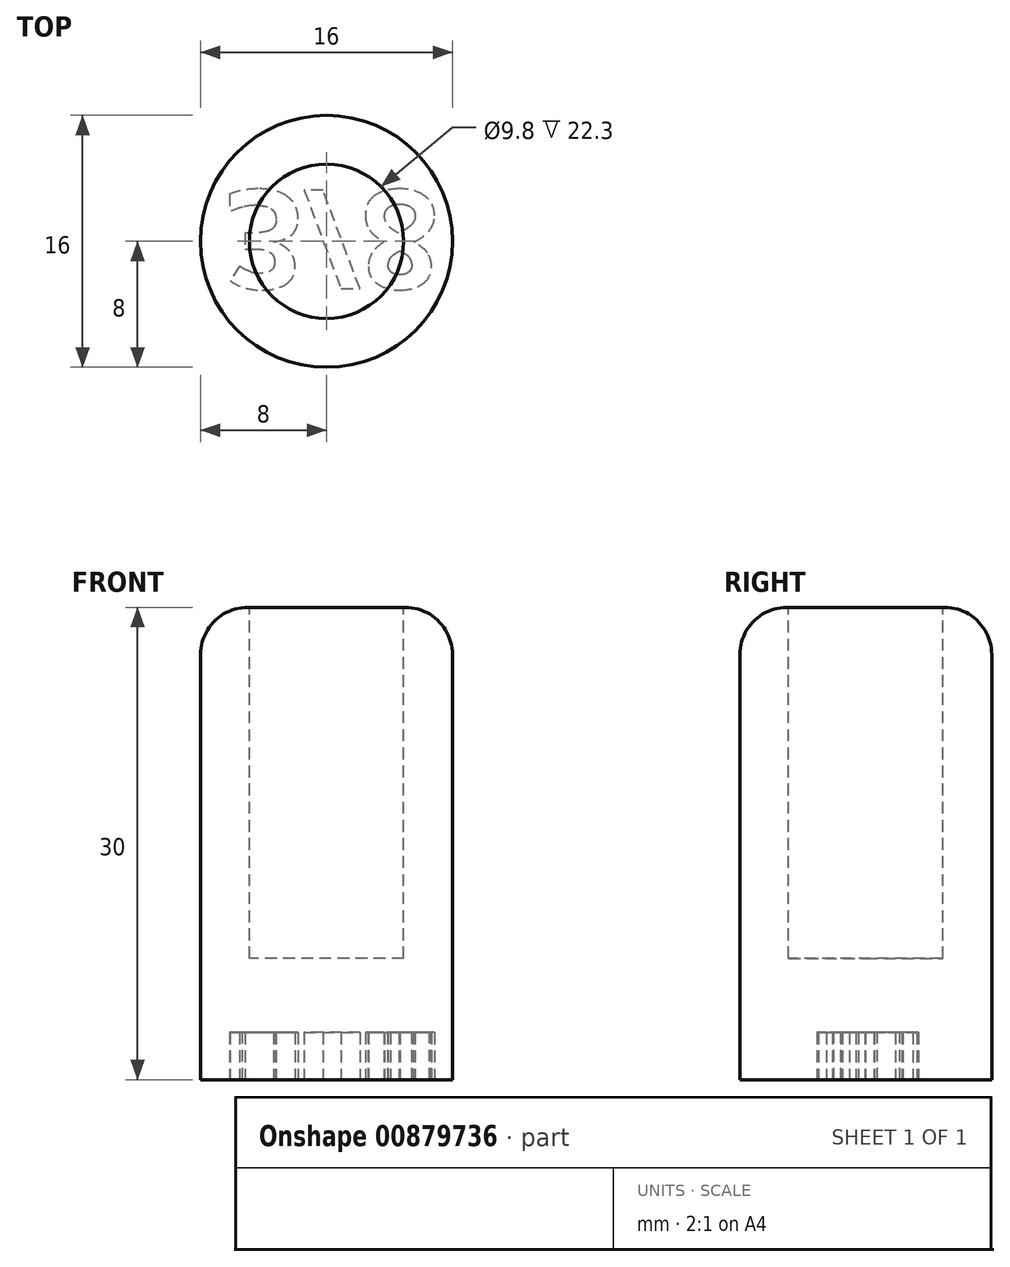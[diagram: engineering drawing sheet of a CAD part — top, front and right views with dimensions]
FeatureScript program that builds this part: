
annotation { "Feature Type Name" : "Feature", "Feature Type Description" : "" }
export const myFeature = defineFeature(function(context is Context, id is Id, definition is map)
    precondition{}
    {
        {
            var Q0;
            Q0=qCreatedBy(makeId("Top.planeOp"),FACE);
            var sketch = newSketch(context, id + "F0", { "sketchPlane" : qUnion([Q0])});
            skCircle(sketch, "E0", {"center": v(0, 0) * mm, "radius": 8 * mm});
            skSolve(sketch);
        }
        {
            var Q0;
            Q0=makeQuery(id+"F0.imprint","IMPRINT",FACE,{"disambiguationData":[TD([[makeQuery(id+"F0.imprint","IMPRINT",EDGE,{"derivedFrom":sQuery(id+"F0.wireOp",EDGE,"E0")}),1.0]])]});
            extrude(context, id + "F1", {"entities" : qUnion([Q0]), "depth" : 30 * mm, "offsetDistance" : 25 * mm});
        }
        {
            var Q0;
            Q0=makeQuery(id+"F1.opExtrude","CAP_FACE",FACE,{"disambiguationData":[OSD([sQuery(id+"F0.wireOp",EDGE,"E0")])],"isStart":false});
            cPlane(context, id + "F2", {"entities" : qUnion([Q0]), "cplaneType" : CPlaneType.OFFSET, "offset" : 0 * mm, "width" : 150 * mm, "height" : 150 * mm});
        }
        {
            var Q0;
            Q0=qCreatedBy(id+"F2.planeOp",FACE);
            var sketch = newSketch(context, id + "F3", { "sketchPlane" : qUnion([Q0])});
            skCircle(sketch, "E1", {"center": v(0, 0) * mm, "radius": 4.9 * mm});
            skSolve(sketch);
        }
        {
            var Q0;
            Q0=qSketchRegion(id+"F3",true);
            extrude(context, id + "F4", {"entities" : qUnion([Q0]), "operationType" : NewBodyOperationType.REMOVE, "oppositeDirection" : true, "depth" : 22.3 * mm, "offsetDistance" : 25 * mm});
        }
        {
            var Q0;
            Q0=makeQuery(id+"F1.opExtrude","CAP_FACE",FACE,{"disambiguationData":[OSD([sQuery(id+"F0.wireOp",EDGE,"E0")])],"isStart":true});
            cPlane(context, id + "F5", {"entities" : qUnion([Q0]), "cplaneType" : CPlaneType.OFFSET, "offset" : 0 * mm, "width" : 150 * mm, "height" : 150 * mm});
        }
        {
            var Q0;
            Q0=qCreatedBy(id+"F5.planeOp",FACE);
            var sketch = newSketch(context, id + "F6", { "sketchPlane" : qUnion([Q0])});
            skLineSegment(sketch, "E2", {"start": v(7.64, 3.07) * mm, "end": v(-6.76, 3.07) * mm, "construction": true});
            skText(sketch, "E3", { "text": "3/8", "fontName": "OpenSans-Bold.ttf"});
            const initialGuessF6  = {"E3": [-0.00648, -0.00325, 1, 0, 0.00632]};
            skSetInitialGuess(sketch, initialGuessF6);
            skSolve(sketch);
        }
        {
            var Q0;
            Q0 = qSketchRegion(id + "F6", true);
            extrude(context, id + "F7", {"entities" : qUnion([Q0]), "operationType" : NewBodyOperationType.REMOVE, "oppositeDirection" : true, "depth" : 3 * mm, "offsetDistance" : 25 * mm});
        }
        {
            var Q0;
            Q0=makeQuery(id+"F1.opExtrude","CAP_EDGE",EDGE,{"disambiguationData":[OSD([sQuery(id+"F0.wireOp",EDGE,"E0")])],"isStart":false});
            fillet(context, id + "F8", {"entities" : qUnion([Q0]), "radius" : 3 * mm, "tangentPropagation" : true, "allowEdgeOverflow" : false});
        }
    });
